# Revit family: Multilift_Savaria
name_source: partatom
category: Specialty Equipment
units: mm (PartAtom-declared; Revit-internal decimal feet)

## family parameters
Always vertical = Yes
Classification Number = 23.50.05.11
Cut with Voids When Loaded = No
Enable Cutting in Views = No
Maintain Annotation Orientation = No
Part Type = Normal
Room Calculation Point = No
Round Connector Dimension = Use Diameter
Shared = No
Work Plane-Based = No

## types (1)
- Multilift_Savaria
    ADA Compliant = Yes
    Assembly Code = D1010310
    Building Code Conformance = [ASME A17.1; NFPA 70][CSA B44; CSA National Electrical Code]
    Capacity (Weight) = 1400.00 lb
    Construction Details = http://www.arcat.com
    Default Elevation = 0' - 0"
    Description = Savaria Concord Hydraulic Passenger Elevator as Specified in 14 40 00
    Expected Lifespan (Years) = 0
    Finish = Metal - Color As Specified
    Green Building-LEED = http://www.arcat.com
    Installation Phase = Interior fixtures and fittings
    Keynote = 14 40 00
    Lift Height = 0' - 0"
    Maintenance Schedule (Months) = 0
    Manufacturer = Savaria Concord
    Manufacturer Fax = 905-791-2222
    Manufacturer Website = http://www.savariaconcord.com
    Model = As Specified in 14 40 00
    Overhead = 0' - 0"
    Pit Depth = 0' - 6 13/16"
    Product Data = http://www.arcat.com
    Product Properties = http://www.arcat.com
    Send Message = http://www.arcat.com
    SpecWizard = http://www.arcat.com
    Specification = http://www.arcat.com
    Stops = 2
    URL = http://www.savariaconcord.com
    Unit Depth = 0' - 0"
    Unit Width = 0' - 0"
    Warranty Duration (Years) = 1

## geometry (parser evidence)
native form markers: Blend x36, Sweep x6
no freeform markers — native parametric forms only
